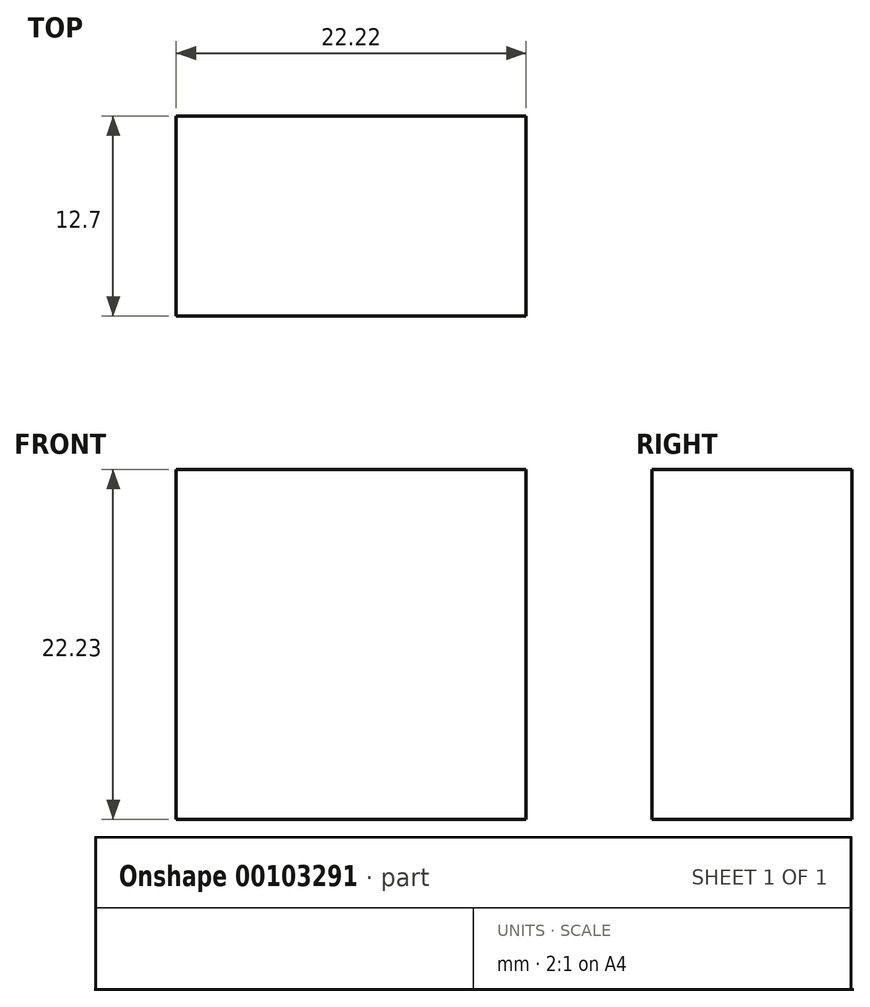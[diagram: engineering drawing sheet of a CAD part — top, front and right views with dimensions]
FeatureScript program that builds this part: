
annotation { "Feature Type Name" : "Feature", "Feature Type Description" : "" }
export const myFeature = defineFeature(function(context is Context, id is Id, definition is map)
    precondition{}
    {
        {
            var Q0;
            Q0=qCreatedBy(makeId("Front.planeOp"),FACE);
            var sketch = newSketch(context, id + "F0", { "sketchPlane" : qUnion([Q0])});
            skLineSegment(sketch, "E0.bottom", {"start": v(1.32, 0) * mm, "end": v(23.54, 0) * mm});
            skLineSegment(sketch, "E0.top", {"start": v(1.32, 22.23) * mm, "end": v(23.54, 22.23) * mm});
            skLineSegment(sketch, "E0.left", {"start": v(1.32, 0) * mm, "end": v(1.32, 22.23) * mm});
            skLineSegment(sketch, "E0.right", {"start": v(23.54, 0) * mm, "end": v(23.54, 22.23) * mm});
            skSolve(sketch);
        }
        {
            var Q0;
            Q0 = qSketchRegion(id + "F0", true);
            var Q1;
            Q1=makeQuery(id+"F0.imprint","IMPRINT",FACE,{"disambiguationData":[TD([[makeQuery(id+"F0.imprint","IMPRINT",EDGE,{"derivedFrom":sQuery(id+"F0.wireOp",EDGE,"E0.bottom")}),1.0]])]});
            extrude(context, id + "F1", {"entities" : qUnion([Q0, Q1]), "depth" : 12.7 * mm});
        }
    });
